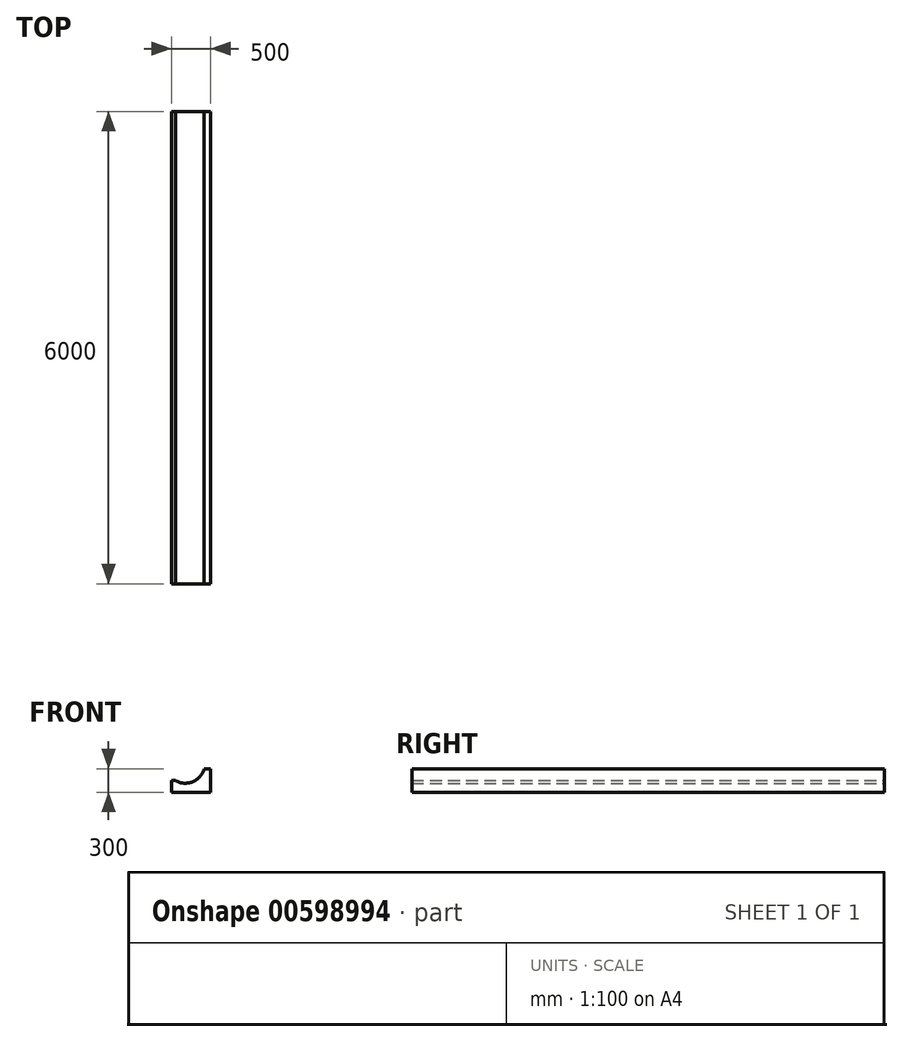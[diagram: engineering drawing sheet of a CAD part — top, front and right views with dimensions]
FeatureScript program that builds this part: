
annotation { "Feature Type Name" : "Feature", "Feature Type Description" : "" }
export const myFeature = defineFeature(function(context is Context, id is Id, definition is map)
    precondition{}
    {
        {
            var Q0;
            Q0=qCreatedBy(makeId("Front.planeOp"),FACE);
            var sketch = newSketch(context, id + "F0", { "sketchPlane" : qUnion([Q0])});
            skLineSegment(sketch, "E0", {"start": v(-175, 0) * mm, "end": v(325, 0) * mm});
            skLineSegment(sketch, "E1", {"start": v(325, 0) * mm, "end": v(325, 300) * mm});
            skLineSegment(sketch, "E2", {"start": v(325, 300) * mm, "end": v(241, 300) * mm});
            skArc(sketch, "E3", {"start": v(-125, 150) * mm, "mid": v(94.8, 135.18) * mm, "end": v(241, 300) * mm});
            skLineSegment(sketch, "E4", {"start": v(-175, 0) * mm, "end": v(-175, 150) * mm});
            skLineSegment(sketch, "E5", {"start": v(-175, 150) * mm, "end": v(-125, 150) * mm});
            skSolve(sketch);
        }
        {
            var Q0;
            Q0 = qSketchRegion(id + "F0", true);
            extrude(context, id + "F1", {"entities" : qUnion([Q0]), "depth" : 6000 * mm, "offsetDistance" : 25 * mm});
        }
    });
